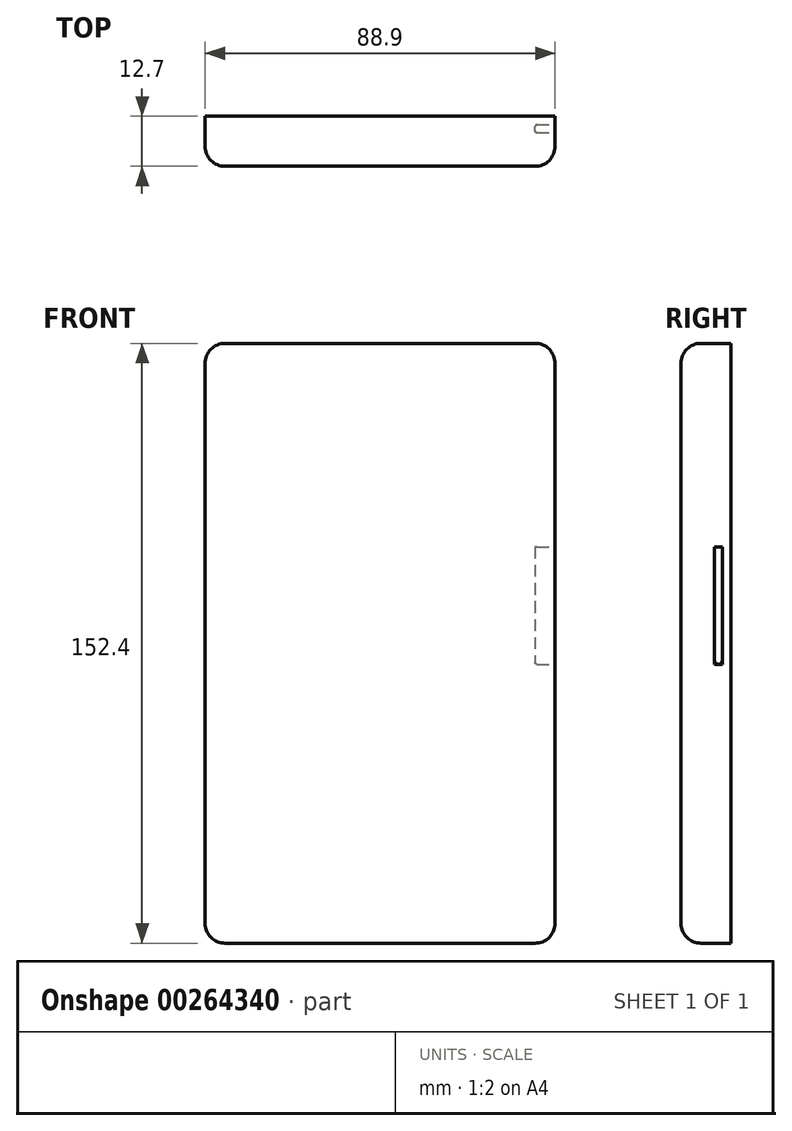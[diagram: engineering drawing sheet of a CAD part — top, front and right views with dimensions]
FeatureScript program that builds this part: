
annotation { "Feature Type Name" : "Feature", "Feature Type Description" : "" }
export const myFeature = defineFeature(function(context is Context, id is Id, definition is map)
    precondition{}
    {
        {
            var Q0;
            Q0=qCreatedBy(makeId("Front.planeOp"),FACE);
            var sketch = newSketch(context, id + "F0", { "sketchPlane" : qUnion([Q0])});
            skLineSegment(sketch, "E0.bottom", {"start": v(-44.45, 76.2) * mm, "end": v(44.45, 76.2) * mm});
            skLineSegment(sketch, "E0.top", {"start": v(-44.45, -76.2) * mm, "end": v(44.45, -76.2) * mm});
            skLineSegment(sketch, "E0.left", {"start": v(-44.45, 76.2) * mm, "end": v(-44.45, -76.2) * mm});
            skLineSegment(sketch, "E0.right", {"start": v(44.45, 76.2) * mm, "end": v(44.45, -76.2) * mm});
            skPoint(sketch, "E0.middle", {"position": v(0, 0) * mm});
            skSolve(sketch);
        }
        {
            var Q0;
            Q0=makeQuery(id+"F0.imprint","IMPRINT",FACE,{"disambiguationData":[TD([[makeQuery(id+"F0.imprint","IMPRINT",EDGE,{"derivedFrom":sQuery(id+"F0.wireOp",EDGE,"E0.bottom")}),-1.0]])]});
            extrude(context, id + "F1", {"entities" : qUnion([Q0]), "endBound" : BoundingType.SYMMETRIC, "depth" : 12.7 * mm});
        }
        {
            var Q0;
            Q0=makeQuery(id+"F1.opExtrude","CAP_FACE",FACE,{"disambiguationData":[OSD([sQuery(id+"F0.wireOp",EDGE,"E0.bottom"),sQuery(id+"F0.wireOp",EDGE,"E0.top"),sQuery(id+"F0.wireOp",EDGE,"E0.left"),sQuery(id+"F0.wireOp",EDGE,"E0.right")])],"isStart":false});
            var Q1;
            Q1=makeQuery(id+"F1.opExtrude","SWEPT_EDGE",EDGE,{"disambiguationData":[OSD([sQuery(id+"F0.wireOp",EDGE,"E0.bottom"),sQuery(id+"F0.wireOp",EDGE,"E0.left")])]});
            var Q2;
            Q2=makeQuery(id+"F1.opExtrude","SWEPT_EDGE",EDGE,{"disambiguationData":[OSD([sQuery(id+"F0.wireOp",EDGE,"E0.top"),sQuery(id+"F0.wireOp",EDGE,"E0.left")])]});
            var Q3;
            Q3=makeQuery(id+"F1.opExtrude","SWEPT_EDGE",EDGE,{"disambiguationData":[OSD([sQuery(id+"F0.wireOp",EDGE,"E0.top"),sQuery(id+"F0.wireOp",EDGE,"E0.right")])]});
            var Q4;
            Q4=makeQuery(id+"F1.opExtrude","SWEPT_EDGE",EDGE,{"disambiguationData":[OSD([sQuery(id+"F0.wireOp",EDGE,"E0.bottom"),sQuery(id+"F0.wireOp",EDGE,"E0.right")])]});
            fillet(context, id + "F2", {"entities" : qUnion([Q0, Q1, Q2, Q3, Q4]), "radius" : 5.08 * mm, "tangentPropagation" : true, "allowEdgeOverflow" : false});
        }
        {
            var Q0;
            Q0=makeQuery(id+"F1.opExtrude","SWEPT_FACE",FACE,{"disambiguationData":[OSD([sQuery(id+"F0.wireOp",EDGE,"E0.right")])]});
            var sketch = newSketch(context, id + "F3", { "sketchPlane" : qUnion([Q0])});
            skLineSegment(sketch, "E1.bottom", {"start": v(2.17, 24.52) * mm, "end": v(4.2, 24.52) * mm});
            skLineSegment(sketch, "E1.top", {"start": v(2.17, -5.35) * mm, "end": v(4.2, -5.35) * mm});
            skLineSegment(sketch, "E1.left", {"start": v(2.17, 24.52) * mm, "end": v(2.17, -5.35) * mm});
            skLineSegment(sketch, "E1.right", {"start": v(4.2, 24.52) * mm, "end": v(4.2, -5.35) * mm});
            skSolve(sketch);
        }
        {
            var Q0;
            Q0 = qSketchRegion(id + "F3", true);
            extrude(context, id + "F4", {"entities" : qUnion([Q0]), "operationType" : NewBodyOperationType.REMOVE, "oppositeDirection" : true, "depth" : 5.08 * mm});
        }
        {
            var Q0;
            Q0=makeQuery(id+"F4.boolean.opBoolean","COPY",EDGE,{"derivedFrom":makeQuery(id+"F4.opExtrude","CAP_EDGE",EDGE,{"disambiguationData":[OSD([sQuery(id+"F3.wireOp",EDGE,"E1.right")])],"isStart":false})});
            var Q1;
            Q1=makeQuery(id+"F4.boolean.opBoolean","COPY",EDGE,{"derivedFrom":makeQuery(id+"F4.opExtrude","CAP_EDGE",EDGE,{"disambiguationData":[OSD([sQuery(id+"F3.wireOp",EDGE,"E1.left")])],"isStart":false})});
            var Q2;
            Q2=makeQuery(id+"F4.boolean.opBoolean","COPY",EDGE,{"derivedFrom":makeQuery(id+"F4.opExtrude","CAP_EDGE",EDGE,{"disambiguationData":[OSD([sQuery(id+"F3.wireOp",EDGE,"E1.top")])],"isStart":false})});
            var Q3;
            Q3=makeQuery(id+"F4.boolean.opBoolean","COPY",EDGE,{"derivedFrom":makeQuery(id+"F4.opExtrude","CAP_EDGE",EDGE,{"disambiguationData":[OSD([sQuery(id+"F3.wireOp",EDGE,"E1.bottom")])],"isStart":true})});
            fillet(context, id + "F5", {"entities" : qUnion([Q0, Q1, Q2, Q3]), "radius" : 0.5 * mm, "tangentPropagation" : true, "allowEdgeOverflow" : false});
        }
    });
